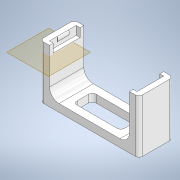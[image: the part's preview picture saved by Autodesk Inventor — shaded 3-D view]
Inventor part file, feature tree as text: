
AUTODESK INVENTOR PART (.ipt)
format: ipt  version: 2021 (Build 250183000, 183)  size: 230,912 bytes
history: mixed  units: in
note: dims shown in document units (in); Inventor stores cm internally (conversion verified against a paired STEP export)
features: projected_geometry x6, extrude x5, sketch x5, fillet x2, mirror x1, plane x1, imported_body x1
ambient origin geometry x8: Origin, YZ Plane, XZ Plane, XY Plane, X Axis, Y Axis, Z Axis, Center Point
bodies: Solid1 (imported_parasolid)
feature tree (21):
  extrude  "Extrusion1"  Depth=0.0984in
  extrude  "Extrusion2"  Depth=0.2362in
  mirror  "Mirror1"
  extrude  "Extrusion3"  Depth=0.3937in TaperAngle=0.0deg
  extrude  "Extrusion4"  Depth=0.1969in
  fillet  "Fillet4"  Radius=0.0197in
  plane  "Work Plane1"
  extrude  "Extrusion6"  Depth=0.2362in
  sketch  "Sketch1"  dims[d0=0.0984in d1=0.0in d3=0.0984in]
  projected_geometry  "Projected Loop1"
  projected_geometry  "Projected Loop2"
  sketch  "Sketch2"  dims[d4=0.2362in d5=0.0in d7=0.0394in]
  projected_geometry  "Projected Loop3"
  sketch  "Sketch3"  dims[d8=0.0394in d9=0.3937in d10=0.7874in d11=0.0in d12=0.0in]
  sketch  "Sketch4"  dims[d14=0.0394in d15=0.0in d16=0.1969in d22=0.0197in d23=0.0in]
  projected_geometry  "Projected Loop4"
  sketch  "Sketch7"  dims[d24=0.0197in d25=0.2362in d17=0.0197in d18=0.0344in d19=0.0197in d20=0.0344in]
  projected_geometry  "Projected Loop5"
  projected_geometry  "Projected Loop6"
  fillet  "Fillet2"  Radius=0.0197in
  imported_body  NMx_Import_Brep_tag  [imported B-rep: ~38 faces, bbox_mm=[52.0, 28.0, 18.0]]
